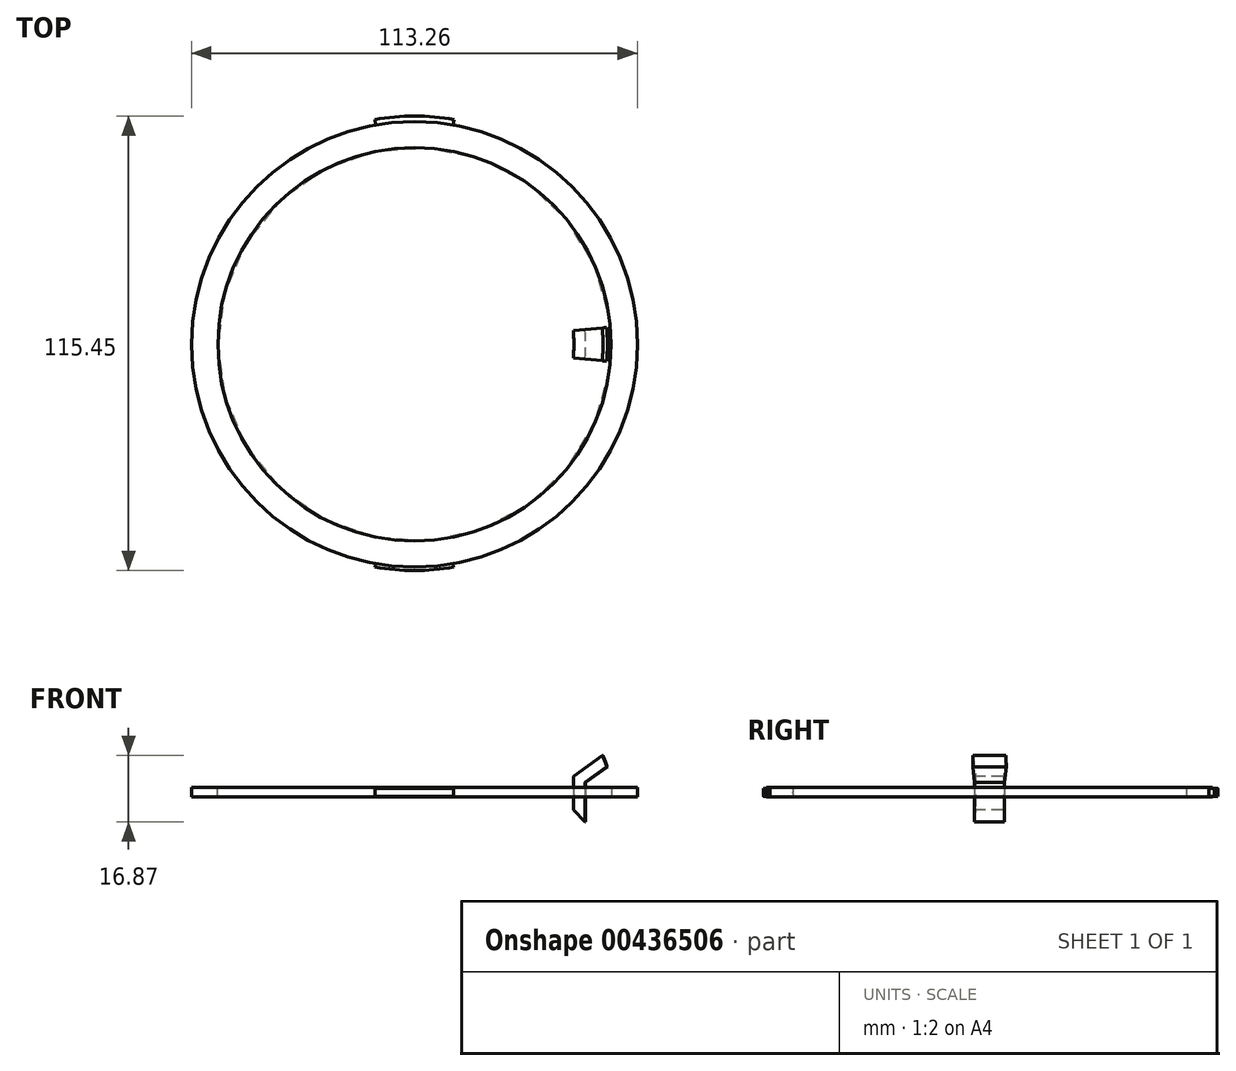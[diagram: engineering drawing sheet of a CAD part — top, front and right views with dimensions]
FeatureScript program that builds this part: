
annotation { "Feature Type Name" : "Feature", "Feature Type Description" : "" }
export const myFeature = defineFeature(function(context is Context, id is Id, definition is map)
    precondition{}
    {
        {
            var Q0;
            Q0=qCreatedBy(makeId("Front.planeOp"),FACE);
            var sketch = newSketch(context, id + "F0", { "sketchPlane" : qUnion([Q0])});
            skEllipticalArc(sketch, "E0", {});
            skFitSpline(sketch, "E1.0", {"points": [v(-53.96, 1.92) * mm, v(-54.03, 0) * mm, v(-53.96, -1.92) * mm, v(-53.67, -4.45) * mm, v(-52.95, -7.57) * mm, v(-51.55, -11.17) * mm, v(-49.65, -14.62) * mm, v(-47.28, -17.88) * mm, v(-44.47, -20.93) * mm, v(-41.77, -23.3) * mm, v(-39.42, -25.07) * mm, v(-37.56, -26.35) * mm, v(-35.6, -27.55) * mm, v(-32.91, -29.06) * mm, v(-29.38, -30.76) * mm, v(-24.9, -32.5) * mm, v(-20.2, -33.94) * mm, v(-15.35, -35.07) * mm, v(-10.34, -35.9) * mm, v(-6.07, -36.3) * mm, v(-2.62, -36.47) * mm, v(0, -36.52) * mm, v(2.6, -36.47) * mm, v(6.06, -36.3) * mm, v(10.33, -35.9) * mm, v(15.34, -35.07) * mm, v(20.2, -33.94) * mm, v(24.89, -32.5) * mm, v(29.37, -30.76) * mm, v(32.9, -29.06) * mm, v(35.6, -27.55) * mm, v(37.55, -26.35) * mm, v(39.41, -25.07) * mm, v(41.77, -23.3) * mm, v(44.46, -20.93) * mm, v(47.27, -17.88) * mm, v(49.65, -14.62) * mm, v(51.55, -11.17) * mm, v(52.94, -7.57) * mm, v(53.66, -4.45) * mm, v(53.95, -1.92) * mm, v(54.02, 0) * mm, v(53.95, 1.92) * mm, v(53.66, 4.45) * mm, v(52.94, 7.57) * mm, v(51.55, 11.17) * mm, v(49.65, 14.62) * mm, v(47.27, 17.88) * mm, v(44.46, 20.93) * mm, v(41.77, 23.3) * mm, v(39.41, 25.07) * mm, v(37.55, 26.35) * mm, v(35.6, 27.55) * mm, v(32.9, 29.06) * mm, v(29.37, 30.76) * mm, v(24.89, 32.5) * mm, v(20.2, 33.94) * mm, v(15.34, 35.07) * mm, v(10.33, 35.9) * mm, v(6.06, 36.3) * mm, v(2.6, 36.47) * mm, v(0, 36.52) * mm, v(-2.62, 36.47) * mm, v(-6.07, 36.3) * mm, v(-10.34, 35.9) * mm, v(-15.35, 35.07) * mm, v(-20.2, 33.94) * mm, v(-24.9, 32.5) * mm, v(-29.38, 30.76) * mm, v(-32.91, 29.06) * mm, v(-35.6, 27.55) * mm, v(-37.56, 26.35) * mm, v(-39.42, 25.07) * mm, v(-41.77, 23.3) * mm, v(-44.47, 20.93) * mm, v(-47.28, 17.88) * mm, v(-49.65, 14.62) * mm, v(-51.55, 11.17) * mm, v(-52.95, 7.57) * mm, v(-53.67, 4.45) * mm, v(-53.96, 1.92) * mm, v(-54.03, 0) * mm, v(-53.96, -1.92) * mm]});
            skLineSegment(sketch, "E2", {"start": v(22.5, -29.02) * mm, "end": v(25, -32.4) * mm});
            skLineSegment(sketch, "E3", {"start": v(0, 0) * mm, "end": v(0, 42.6) * mm});
            skEllipticalArc(sketch, "E4", {});
            skLineSegment(sketch, "E5", {"start": v(49, 6.48) * mm, "end": v(43.49, 2.5) * mm});
            skLineSegment(sketch, "E6", {"start": v(43.49, 2.5) * mm, "end": v(43.49, -7.5) * mm});
            skLineSegment(sketch, "E7.0", {"start": v(40.49, 4.04) * mm, "end": v(40.49, -4.5) * mm});
            skLineSegment(sketch, "E7.1", {"start": v(47.88, 9.37) * mm, "end": v(40.49, 4.04) * mm});
            skLineSegment(sketch, "E8", {"start": v(40.49, -4.5) * mm, "end": v(43.49, -7.5) * mm});
            skFitSpline(sketch, "E9", {"points": [v(-53.95, 1.92) * mm, v(-54.02, 0) * mm, v(-53.95, -1.92) * mm, v(-53.66, -4.45) * mm, v(-52.94, -7.57) * mm, v(-51.55, -11.17) * mm, v(-49.65, -14.62) * mm, v(-47.27, -17.88) * mm, v(-44.46, -20.93) * mm, v(-41.77, -23.3) * mm, v(-39.41, -25.07) * mm, v(-37.55, -26.35) * mm, v(-35.6, -27.55) * mm, v(-32.9, -29.06) * mm, v(-29.37, -30.76) * mm, v(-24.89, -32.5) * mm, v(-20.2, -33.94) * mm, v(-15.34, -35.07) * mm, v(-10.33, -35.89) * mm, v(-6.07, -36.3) * mm, v(-2.61, -36.47) * mm, v(0, -36.51) * mm, v(2.61, -36.47) * mm, v(6.07, -36.3) * mm, v(10.33, -35.89) * mm, v(15.34, -35.07) * mm, v(20.2, -33.94) * mm, v(24.89, -32.5) * mm, v(29.37, -30.76) * mm, v(32.9, -29.06) * mm, v(35.6, -27.55) * mm, v(37.55, -26.35) * mm, v(39.41, -25.07) * mm, v(41.77, -23.3) * mm, v(44.46, -20.93) * mm, v(47.27, -17.88) * mm, v(49.65, -14.62) * mm, v(51.55, -11.17) * mm, v(52.94, -7.57) * mm, v(53.66, -4.45) * mm, v(53.95, -1.92) * mm, v(54.02, 0) * mm, v(53.95, 1.92) * mm, v(53.66, 4.45) * mm, v(52.94, 7.57) * mm, v(51.55, 11.17) * mm, v(49.65, 14.62) * mm, v(47.27, 17.88) * mm, v(44.46, 20.93) * mm, v(41.77, 23.3) * mm, v(39.41, 25.07) * mm, v(37.55, 26.35) * mm, v(35.6, 27.55) * mm, v(32.9, 29.06) * mm, v(29.37, 30.76) * mm, v(24.89, 32.5) * mm, v(20.2, 33.94) * mm, v(15.34, 35.07) * mm, v(10.33, 35.89) * mm, v(6.07, 36.3) * mm, v(2.61, 36.47) * mm, v(0, 36.51) * mm, v(-2.61, 36.47) * mm, v(-6.07, 36.3) * mm, v(-10.33, 35.89) * mm, v(-15.34, 35.07) * mm, v(-20.2, 33.94) * mm, v(-24.89, 32.5) * mm, v(-29.37, 30.76) * mm, v(-32.9, 29.06) * mm, v(-35.6, 27.55) * mm, v(-37.55, 26.35) * mm, v(-39.41, 25.07) * mm, v(-41.77, 23.3) * mm, v(-44.46, 20.93) * mm, v(-47.27, 17.88) * mm, v(-49.65, 14.62) * mm, v(-51.55, 11.17) * mm, v(-52.94, 7.57) * mm, v(-53.66, 4.45) * mm, v(-53.95, 1.92) * mm, v(-54.02, 0) * mm, v(-53.95, -1.92) * mm]});
            skLineSegment(sketch, "E10.bottom", {"start": v(48.48, 1.2) * mm, "end": v(56.63, 1.2) * mm});
            skLineSegment(sketch, "E10.top", {"start": v(48.48, -1.2) * mm, "end": v(56.63, -1.2) * mm});
            skLineSegment(sketch, "E10.left", {"start": v(48.48, 1.2) * mm, "end": v(48.48, -1.2) * mm});
            skLineSegment(sketch, "E10.right", {"start": v(56.63, 1.2) * mm, "end": v(56.63, -1.2) * mm});
            const initialGuessF0  = {"E0": [0, 0, -1, 0, 0.05, 0.0325, 2.0375616658421927, 3.342333341523028], "E4": [-4.042148134937584e-06, 0, -1, 0, 0.0500039609848886, 0.0325025746401776, 3.3423172231012304, 4.712308143825751]};
            skSetInitialGuess(sketch, initialGuessF0);
            skSolve(sketch);
        }
        {
            var Q0;
            {var subQ0=sQuery(id+"F0.wireOp",EDGE,"E5");Q0=makeQuery(id+"F0.imprint","IMPRINT",FACE,{"disambiguationData":[TD([[makeQuery(id+"F0.imprint","IMPRINT",EDGE,{"derivedFrom":subQ0}),-1.0]])]});}
            var Q1;
            Q1=sQuery(id+"F0.wireOp",EDGE,"E3");
            revolve(context, id + "F1", {"entities" : qUnion([Q0]), "axis" : qUnion([Q1]), "revolveType" : RevolveType.SYMMETRIC, "angle" : 10 * degree});
        }
        {
            var Q0;
            {var subQ0=sQuery(id+"F0.wireOp",EDGE,"E4");var subQ1=sQuery(id+"F0.wireOp",EDGE,"E3");var subQ2=makeQuery(id+"F0.imprint","INTERSECT",VERTEX,{"derivedFrom":[subQ1,subQ0]});Q0=makeQuery(id+"F0.imprint","IMPRINT",FACE,{"disambiguationData":[TD([[makeQuery(id+"F0.imprint","IMPRINT",EDGE,{"disambiguationData":[TD([[subQ2,-1.0]])],"derivedFrom":subQ1}),-1.0]])]});}
            var Q1;
            {var subQ0=sQuery(id+"F0.wireOp",EDGE,"E2");Q1=makeQuery(id+"F0.imprint","IMPRINT",FACE,{"disambiguationData":[TD([[makeQuery(id+"F0.imprint","IMPRINT",EDGE,{"derivedFrom":subQ0}),1.0]])]});}
            var Q2;
            {var subQ1=sQuery(id+"F0.wireOp",EDGE,"E0");var subQ7=sQuery(id+"F0.wireOp",EDGE,"E10.top");var subQ9=makeQuery(id+"F0.imprint","INTERSECT",VERTEX,{"derivedFrom":[subQ1,subQ7]});Q2=makeQuery(id+"F0.imprint","IMPRINT",FACE,{"disambiguationData":[TD([[makeQuery(id+"F0.imprint","IMPRINT",EDGE,{"disambiguationData":[TD([[subQ9,-1.0]])],"derivedFrom":subQ1}),-1.0]])]});}
            var Q3;
            Q3=sQuery(id+"F0.wireOp",EDGE,"E3");
            revolve(context, id + "F2", {"operationType" : NewBodyOperationType.ADD, "entities" : qUnion([Q0, Q1, Q2]), "axis" : qUnion([Q3]), "revolveType" : RevolveType.FULL});
        }
        {
            var Q0;
            {var subQ5=sQuery(id+"F0.wireOp",EDGE,"E10.left");Q0=makeQuery(id+"F0.imprint","IMPRINT",FACE,{"disambiguationData":[TD([[makeQuery(id+"F0.imprint","IMPRINT",EDGE,{"derivedFrom":subQ5}),1.0]])]});}
            var Q1;
            {var subQ1=sQuery(id+"F0.wireOp",EDGE,"E0");var subQ7=sQuery(id+"F0.wireOp",EDGE,"E10.top");var subQ9=makeQuery(id+"F0.imprint","INTERSECT",VERTEX,{"derivedFrom":[subQ1,subQ7]});Q1=makeQuery(id+"F0.imprint","IMPRINT",FACE,{"disambiguationData":[TD([[makeQuery(id+"F0.imprint","IMPRINT",EDGE,{"disambiguationData":[TD([[subQ9,-1.0]])],"derivedFrom":subQ1}),-1.0]])]});}
            var Q2;
            {var subQ0=sQuery(id+"F0.wireOp",EDGE,"E10.right");Q2=makeQuery(id+"F0.imprint","IMPRINT",FACE,{"disambiguationData":[TD([[makeQuery(id+"F0.imprint","IMPRINT",EDGE,{"derivedFrom":subQ0}),-1.0]])]});}
            extrude(context, id + "F3", {"entities" : qUnion([Q0, Q1, Q2]), "endBound" : BoundingType.SYMMETRIC, "depth" : 2 * mm});
        }
        {
            var Q0;
            Q0=makeQuery(id+"F3.opExtrude","SWEPT_BODY",BODY,{"disambiguationData":[OSD([sQuery(id+"F0.wireOp",EDGE,"E10.bottom"),sQuery(id+"F0.wireOp",EDGE,"E10.top"),sQuery(id+"F0.wireOp",EDGE,"E10.left"),sQuery(id+"F0.wireOp",EDGE,"E10.right")])]});
            var Q1;
            Q1=makeQuery(id+"F1.opRevolve","SWEPT_BODY",BODY,{"disambiguationData":[OSD([sQuery(id+"F0.wireOp",EDGE,"E4"),sQuery(id+"F0.wireOp",EDGE,"E5"),sQuery(id+"F0.wireOp",EDGE,"E6"),sQuery(id+"F0.wireOp",EDGE,"E7.0"),sQuery(id+"F0.wireOp",EDGE,"E7.1"),sQuery(id+"F0.wireOp",EDGE,"E8")])]});
            booleanBodies(context, id + "F4", {"operationType" : BooleanOperationType.SUBTRACTION, "tools" : qUnion([Q0]), "targets" : qUnion([Q1])});
        }
        {
            var Q0;
            Q0=qCreatedBy(makeId("Right.planeOp"),FACE);
            var sketch = newSketch(context, id + "F5", { "sketchPlane" : qUnion([Q0])});
            skLineSegment(sketch, "E11.bottom", {"start": v(-52.45, -1) * mm, "end": v(-57.45, -1) * mm});
            skLineSegment(sketch, "E11.top", {"start": v(-52.45, 1) * mm, "end": v(-57.45, 1) * mm});
            skLineSegment(sketch, "E11.left", {"start": v(-52.45, -1) * mm, "end": v(-52.45, 1) * mm});
            skLineSegment(sketch, "E11.right", {"start": v(-57.45, -1) * mm, "end": v(-57.45, 1) * mm});
            skLineSegment(sketch, "E12.bottom", {"start": v(53, -1) * mm, "end": v(58, -1) * mm});
            skLineSegment(sketch, "E12.top", {"start": v(53, 1) * mm, "end": v(58, 1) * mm});
            skLineSegment(sketch, "E12.left", {"start": v(53, -1) * mm, "end": v(53, 1) * mm});
            skLineSegment(sketch, "E12.right", {"start": v(58, -1) * mm, "end": v(58, 1) * mm});
            skSolve(sketch);
        }
        {
            var Q0;
            Q0 = qSketchRegion(id + "F5", true);
            var Q1;
            Q1=sQuery(id+"F0.wireOp",EDGE,"E3");
            revolve(context, id + "F6", {"operationType" : NewBodyOperationType.ADD, "entities" : qUnion([Q0]), "axis" : qUnion([Q1]), "revolveType" : RevolveType.SYMMETRIC, "angle" : 20 * degree});
        }
    });
